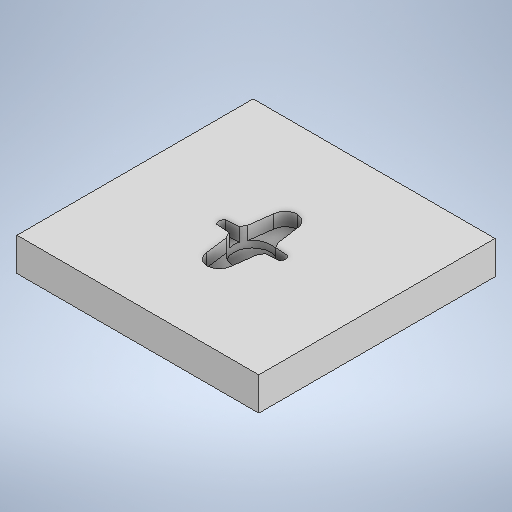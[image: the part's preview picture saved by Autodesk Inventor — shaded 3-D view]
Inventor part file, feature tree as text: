
AUTODESK INVENTOR PART (.ipt)
format: ipt  version: 2025.1 (Build 291241000, 241)  size: 250,880 bytes
history: native  units: in
note: dims shown in document units (in); Inventor stores cm internally (conversion verified against a paired STEP export)
features: extrude x3, sketch x3
ambient origin geometry x8: Origin, YZ Plane, XZ Plane, XY Plane, X Axis, Y Axis, Z Axis, Center Point
bodies: Solid1 (feature_tree)
feature tree (6):
  extrude  "Extrusion1"  Depth=0.5in
  extrude  "Extrusion2"  Depth=0.08in
  extrude  "Extrusion3"  Depth=0.09in
  sketch  "Sketch1"  dims[d0=0.5in d1=0.0in d12=0.18in]
  sketch  "Sketch2"  dims[d16=0.18in d20=0.08in]
  sketch  "Sketch3"  dims[d21=0.08in d22=0.09in d25=0.08in d28=0.2in d29=0.0in d30=0.56in d31=0.3in d32=0.0in d33=0.0344in]
